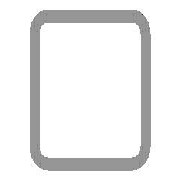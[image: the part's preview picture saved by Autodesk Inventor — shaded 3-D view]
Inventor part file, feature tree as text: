
AUTODESK INVENTOR PART (.ipt)
format: ipt  version: 2025 (Build 290162010, 162A)  size: 133,632 bytes
history: native  units: mm (DEFAULTED — no unit token found)
features: other x4, sketch x1, plane x1
ambient origin geometry x8: Origin, YZ Plane, XZ Plane, XY Plane, X Axis, Y Axis, Z Axis, Center Point
bodies: Solid1 (feature_tree), Body (feature_tree)
feature tree (6):
  parser-record x1  (decoder bookkeeping rows leaked as tree rows — omitted from the tree; the rows remain in map.json)
  other  "Driven Length"
  other  "Start Plane"
  other  "End Plane"
  sketch  "Sketch3"  dims[d3=898.0mm d4=0.0mm d7=4.0mm d9=40.0mm d11=40.0mm d12=2.0mm d13=40.0mm d14=938.0mm d15=20.0mm d16=20.0mm d17=90.0deg d18=898.0mm]
  plane  "Work Plane3"
